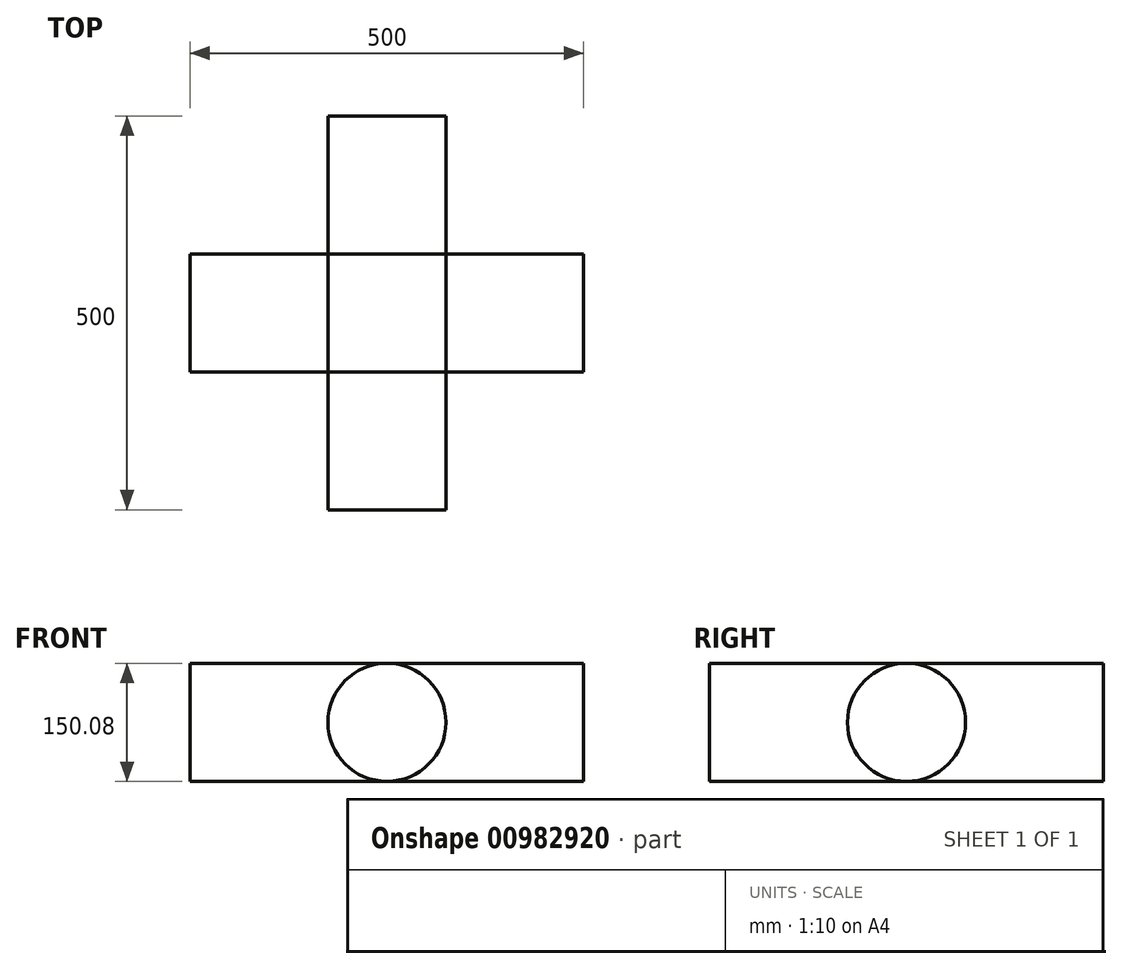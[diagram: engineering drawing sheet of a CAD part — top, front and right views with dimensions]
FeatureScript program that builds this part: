
annotation { "Feature Type Name" : "Feature", "Feature Type Description" : "" }
export const myFeature = defineFeature(function(context is Context, id is Id, definition is map)
    precondition{}
    {
        {
            var Q0;
            Q0=qCreatedBy(makeId("Front.planeOp"),FACE);
            var sketch = newSketch(context, id + "F0", { "sketchPlane" : qUnion([Q0])});
            skCircle(sketch, "E0", {"center": v(0, 0) * mm, "radius": 75 * mm});
            skSolve(sketch);
        }
        {
            var Q0;
            Q0 = qSketchRegion(id + "F0", true);
            var Q1;
            Q1=sQuery(id+"F0.wireOp",EDGE,"E0");
            extrude(context, id + "F1", {"entities" : qUnion([Q0]), "bodyType" : ToolBodyType.SURFACE, "surfaceEntities" : qUnion([Q1]), "endBound" : BoundingType.SYMMETRIC, "depth" : 500 * mm, "offsetDistance" : 25 * mm});
        }
        {
            var Q0;
            Q0=qCreatedBy(makeId("Right.planeOp"),FACE);
            var sketch = newSketch(context, id + "F2", { "sketchPlane" : qUnion([Q0])});
            skCircle(sketch, "E1", {"center": v(0, 0) * mm, "radius": 75.04 * mm});
            skSolve(sketch);
        }
        {
            var Q0;
            Q0 = qSketchRegion(id + "F2", true);
            var Q1;
            Q1=sQuery(id+"F2.wireOp",EDGE,"E1");
            extrude(context, id + "F3", {"entities" : qUnion([Q0]), "bodyType" : ToolBodyType.SURFACE, "surfaceEntities" : qUnion([Q1]), "endBound" : BoundingType.SYMMETRIC, "depth" : 500 * mm, "offsetDistance" : 25 * mm});
        }
    });
